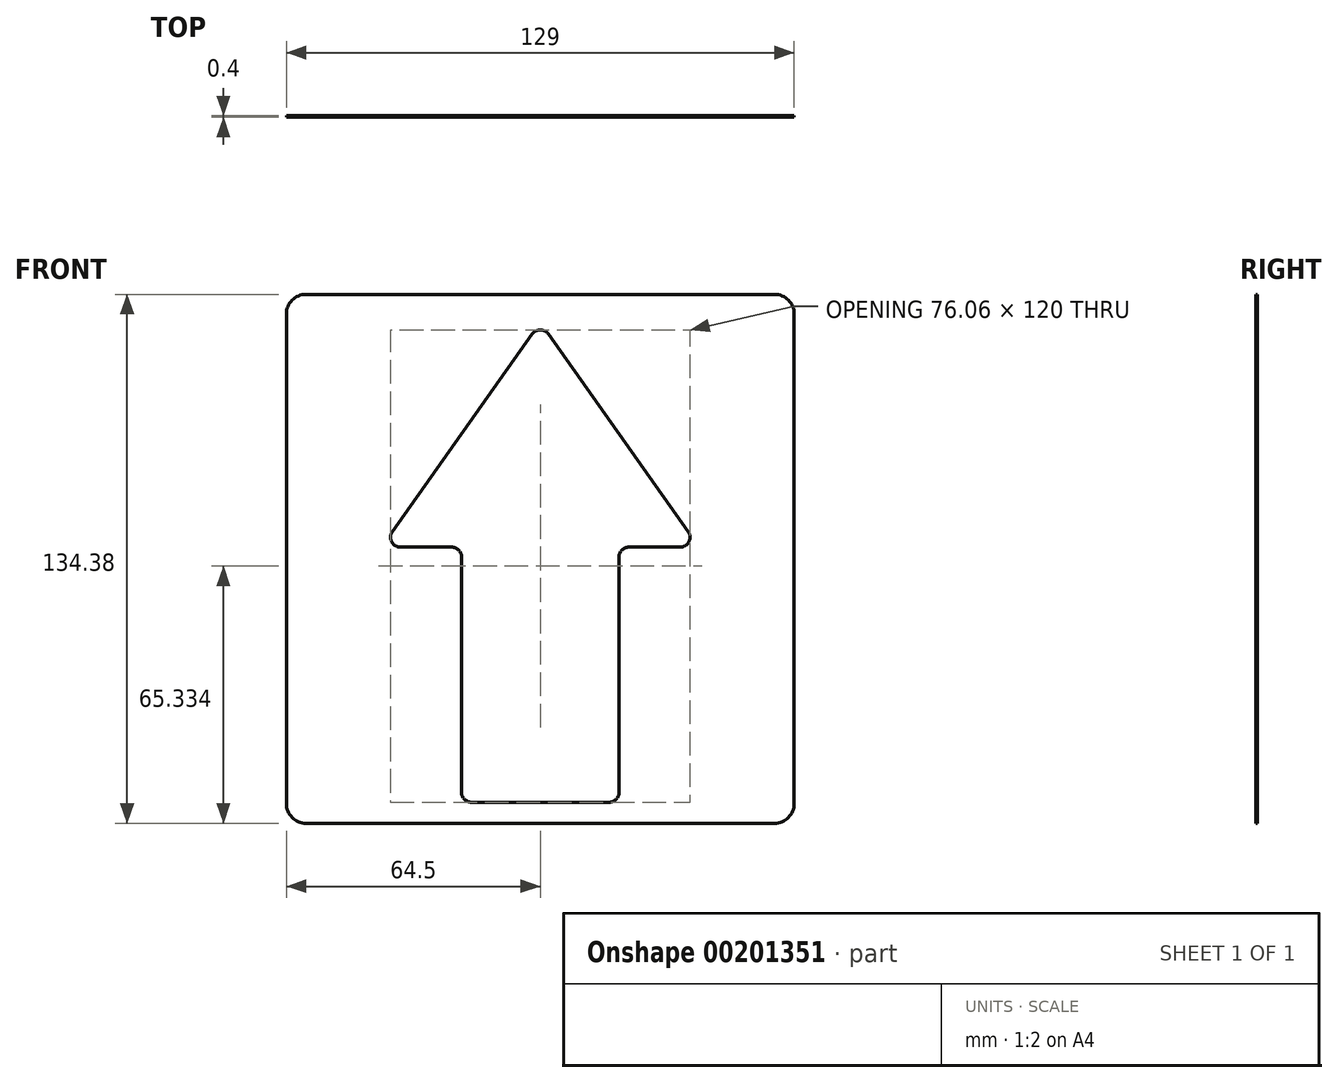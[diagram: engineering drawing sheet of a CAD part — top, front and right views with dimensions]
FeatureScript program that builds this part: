
annotation { "Feature Type Name" : "Feature", "Feature Type Description" : "" }
export const myFeature = defineFeature(function(context is Context, id is Id, definition is map)
    precondition{}
    {
        {
            var Q0;
            Q0=qCreatedBy(makeId("Front.planeOp"),FACE);
            var sketch = newSketch(context, id + "F0", { "sketchPlane" : qUnion([Q0])});
            skLineSegment(sketch, "E0", {"start": v(0, 60) * mm, "end": v(0, -61.86) * mm, "construction": true});
            skLineSegment(sketch, "E1", {"start": v(0, -61.86) * mm, "end": v(-17.46, -61.86) * mm});
            skLineSegment(sketch, "E2", {"start": v(-22.54, 2.96) * mm, "end": v(-35.5, 2.96) * mm});
            skLineSegment(sketch, "E3", {"start": v(-37.57, 6.97) * mm, "end": v(-2.07, 57.07) * mm});
            skLineSegment(sketch, "E4", {"start": v(-20, 0.42) * mm, "end": v(-20, -59.32) * mm});
            skPoint(sketch, "E5.visualSharp", {"position": v(-40.4, 2.96) * mm});
            skArc(sketch, "E5.filletArc", {"start": v(-37.57, 6.97) * mm, "mid": v(-37.75, 4.33) * mm, "end": v(-35.5, 2.96) * mm});
            skLineSegment(sketch, "E6.MirrorCS", {"start": v(37.57, 6.97) * mm, "end": v(2.07, 57.07) * mm});
            skArc(sketch, "E7.MirrorCS", {"start": v(37.57, 6.97) * mm, "mid": v(37.75, 4.33) * mm, "end": v(35.5, 2.96) * mm});
            skLineSegment(sketch, "E8.MirrorCS", {"start": v(22.54, 2.96) * mm, "end": v(35.5, 2.96) * mm});
            skLineSegment(sketch, "E9.MirrorCS", {"start": v(20, 0.42) * mm, "end": v(20, -59.32) * mm});
            skLineSegment(sketch, "E10.MirrorCS", {"start": v(0, -61.86) * mm, "end": v(17.46, -61.86) * mm});
            skPoint(sketch, "E11.visualSharp", {"position": v(0, 60) * mm});
            skArc(sketch, "E11.filletArc", {"start": v(2.07, 57.07) * mm, "mid": v(0, 58.14) * mm, "end": v(-2.07, 57.07) * mm});
            skPoint(sketch, "E12.visualSharp", {"position": v(-20, -61.86) * mm});
            skArc(sketch, "E12.filletArc", {"start": v(-20, -59.32) * mm, "mid": v(-19.26, -61.11) * mm, "end": v(-17.46, -61.86) * mm});
            skPoint(sketch, "E13.visualSharp", {"position": v(20, -61.86) * mm});
            skArc(sketch, "E13.filletArc", {"start": v(17.46, -61.86) * mm, "mid": v(19.26, -61.11) * mm, "end": v(20, -59.32) * mm});
            skPoint(sketch, "E14.visualSharp", {"position": v(20, 2.96) * mm});
            skArc(sketch, "E14.filletArc", {"start": v(22.54, 2.96) * mm, "mid": v(20.74, 2.22) * mm, "end": v(20, 0.42) * mm});
            skPoint(sketch, "E15.visualSharp", {"position": v(-20, 2.96) * mm});
            skArc(sketch, "E15.filletArc", {"start": v(-20, 0.42) * mm, "mid": v(-20.74, 2.22) * mm, "end": v(-22.54, 2.96) * mm});
            skLineSegment(sketch, "E16.bottom", {"start": v(64.5, -67.2) * mm, "end": v(-64.5, -67.2) * mm});
            skLineSegment(sketch, "E16.top", {"start": v(64.5, 67.2) * mm, "end": v(-64.5, 67.2) * mm});
            skLineSegment(sketch, "E16.left", {"start": v(64.5, -67.2) * mm, "end": v(64.5, 67.2) * mm});
            skLineSegment(sketch, "E16.right", {"start": v(-64.5, -67.2) * mm, "end": v(-64.5, 67.2) * mm});
            skPoint(sketch, "E16.middle", {"position": v(0, 0) * mm});
            skSolve(sketch);
        }
        {
            var Q0;
            Q0=makeQuery(id+"F0.imprint","IMPRINT",FACE,{"disambiguationData":[TD([[makeQuery(id+"F0.imprint","IMPRINT",EDGE,{"derivedFrom":sQuery(id+"F0.wireOp",EDGE,"E1")}),1.0]])]});
            extrude(context, id + "F1", {"entities" : qUnion([Q0]), "depth" : 0.4 * mm});
        }
        {
            var Q0;
            Q0=makeQuery(id+"F1.opExtrude","SWEPT_EDGE",EDGE,{"disambiguationData":[OSD([sQuery(id+"F0.wireOp",EDGE,"E16.top"),sQuery(id+"F0.wireOp",EDGE,"E16.right")])]});
            var Q1;
            Q1=makeQuery(id+"F1.opExtrude","SWEPT_EDGE",EDGE,{"disambiguationData":[OSD([sQuery(id+"F0.wireOp",EDGE,"E16.top"),sQuery(id+"F0.wireOp",EDGE,"E16.left")])]});
            var Q2;
            Q2=makeQuery(id+"F1.opExtrude","SWEPT_EDGE",EDGE,{"disambiguationData":[OSD([sQuery(id+"F0.wireOp",EDGE,"E16.bottom"),sQuery(id+"F0.wireOp",EDGE,"E16.left")])]});
            var Q3;
            Q3=makeQuery(id+"F1.opExtrude","SWEPT_EDGE",EDGE,{"disambiguationData":[OSD([sQuery(id+"F0.wireOp",EDGE,"E16.bottom"),sQuery(id+"F0.wireOp",EDGE,"E16.right")])]});
            fillet(context, id + "F2", {"entities" : qUnion([Q0, Q1, Q2, Q3]), "radius" : 5 * mm, "tangentPropagation" : true, "allowEdgeOverflow" : false});
        }
    });
